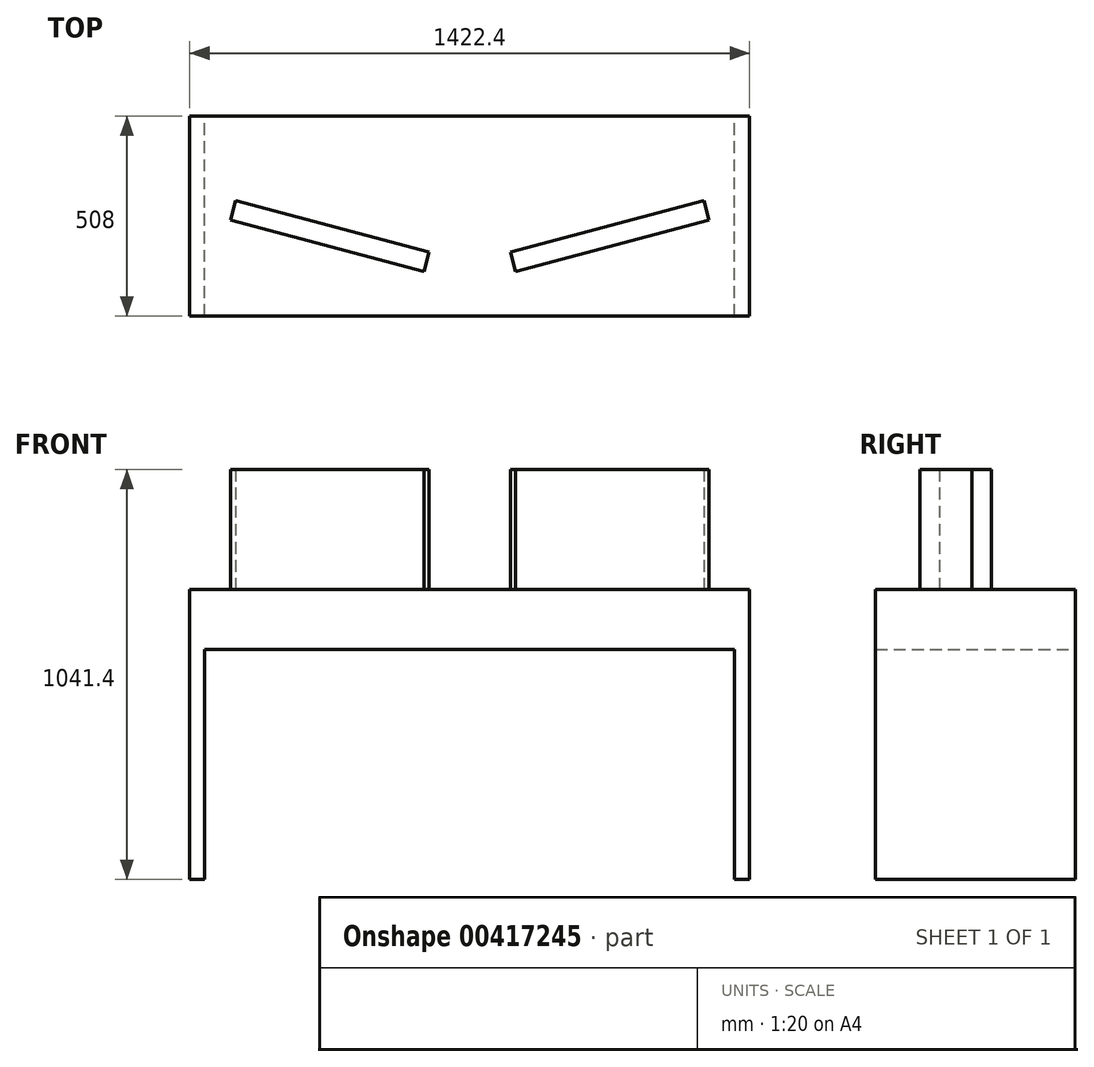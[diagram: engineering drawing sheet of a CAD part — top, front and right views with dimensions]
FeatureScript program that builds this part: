
annotation { "Feature Type Name" : "Feature", "Feature Type Description" : "" }
export const myFeature = defineFeature(function(context is Context, id is Id, definition is map)
    precondition{}
    {
        {
            var Q0;
            Q0=qCreatedBy(makeId("Top.planeOp"),FACE);
            var sketch = newSketch(context, id + "F0", { "sketchPlane" : qUnion([Q0])});
            skLineSegment(sketch, "E0.bottom", {"start": v(0, 0) * mm, "end": v(38.1, 0) * mm});
            skLineSegment(sketch, "E0.top", {"start": v(0, 508) * mm, "end": v(38.1, 508) * mm});
            skLineSegment(sketch, "E0.left", {"start": v(0, 0) * mm, "end": v(0, 508) * mm});
            skLineSegment(sketch, "E0.right", {"start": v(38.1, 0) * mm, "end": v(38.1, 508) * mm});
            skLineSegment(sketch, "E1.bottom", {"start": v(1384.3, 0) * mm, "end": v(1422.4, 0) * mm});
            skLineSegment(sketch, "E1.top", {"start": v(1384.3, 508) * mm, "end": v(1422.4, 508) * mm});
            skLineSegment(sketch, "E1.left", {"start": v(1384.3, 0) * mm, "end": v(1384.3, 508) * mm});
            skLineSegment(sketch, "E1.right", {"start": v(1422.4, 0) * mm, "end": v(1422.4, 508) * mm});
            skLineSegment(sketch, "E2.bottom", {"start": v(0, 0) * mm, "end": v(1422.4, 0) * mm, "construction": true});
            skLineSegment(sketch, "E2.top", {"start": v(0, 508) * mm, "end": v(1422.4, 508) * mm, "construction": true});
            skLineSegment(sketch, "E2.left", {"start": v(0, 0) * mm, "end": v(0, 508) * mm, "construction": true});
            skLineSegment(sketch, "E2.right", {"start": v(1422.4, 0) * mm, "end": v(1422.4, 508) * mm, "construction": true});
            skSolve(sketch);
        }
        {
            var Q0;
            Q0=makeQuery(id+"F0.imprint","IMPRINT",FACE,{"disambiguationData":[TD([[makeQuery(id+"F0.imprint","IMPRINT",EDGE,{"derivedFrom":sQuery(id+"F0.wireOp",EDGE,"E0.bottom")}),1.0]])]});
            var Q1;
            Q1=makeQuery(id+"F0.imprint","IMPRINT",FACE,{"disambiguationData":[TD([[makeQuery(id+"F0.imprint","IMPRINT",EDGE,{"derivedFrom":sQuery(id+"F0.wireOp",EDGE,"E1.bottom")}),1.0]])]});
            extrude(context, id + "F1", {"entities" : qUnion([Q0, Q1]), "depth" : 584.2 * mm});
        }
        {
            var Q0;
            Q0=makeQuery(id+"F1.opExtrude","CAP_FACE",FACE,{"disambiguationData":[OSD([sQuery(id+"F0.wireOp",EDGE,"E0.bottom"),sQuery(id+"F0.wireOp",EDGE,"E0.top"),sQuery(id+"F0.wireOp",EDGE,"E0.left"),sQuery(id+"F0.wireOp",EDGE,"E0.right")])],"isStart":false});
            var sketch = newSketch(context, id + "F2", { "sketchPlane" : qUnion([Q0])});
            skLineSegment(sketch, "E3.bottom", {"start": v(0, 0) * mm, "end": v(1422.4, 0) * mm});
            skLineSegment(sketch, "E3.top", {"start": v(0, 508) * mm, "end": v(1422.4, 508) * mm});
            skLineSegment(sketch, "E3.left", {"start": v(0, 0) * mm, "end": v(0, 508) * mm});
            skLineSegment(sketch, "E3.right", {"start": v(1422.4, 0) * mm, "end": v(1422.4, 508) * mm});
            skPoint(sketch, "E4.0", {"position": v(1422.4, 508) * mm});
            skSolve(sketch);
        }
        {
            var Q0;
            {var subQ2=sQuery(id+"F2.wireOp",EDGE,"E3.right");Q0=makeQuery(id+"F2.imprint","IMPRINT",FACE,{"disambiguationData":[TD([[makeQuery(id+"F2.imprint","IMPRINT",EDGE,{"derivedFrom":subQ2}),1.0]])]});}
            var Q1;
            {var subQ0=sQuery(id+"F2.wireOp",EDGE,"E3.left");Q1=makeQuery(id+"F2.imprint","IMPRINT",FACE,{"disambiguationData":[TD([[makeQuery(id+"F2.imprint","IMPRINT",EDGE,{"derivedFrom":subQ0}),-1.0]])]});}
            extrude(context, id + "F3", {"entities" : qUnion([Q0, Q1]), "operationType" : NewBodyOperationType.ADD, "depth" : 152.4 * mm});
        }
        {
            var Q0;
            Q0=makeQuery(id+"F3.opExtrude","CAP_FACE",FACE,{"disambiguationData":[OSD([sQuery(id+"F2.wireOp",EDGE,"E3.bottom"),sQuery(id+"F2.wireOp",EDGE,"E3.top"),sQuery(id+"F2.wireOp",EDGE,"E3.left"),sQuery(id+"F2.wireOp",EDGE,"E3.right")])],"isStart":false});
            var sketch = newSketch(context, id + "F4", { "sketchPlane" : qUnion([Q0])});
            skLineSegment(sketch, "E5.bottom", {"start": v(607.52, 162) * mm, "end": v(116.83, 293.47) * mm});
            skLineSegment(sketch, "E5.top", {"start": v(594.37, 112.93) * mm, "end": v(103.68, 244.4) * mm});
            skLineSegment(sketch, "E5.left", {"start": v(607.52, 162) * mm, "end": v(594.37, 112.93) * mm});
            skLineSegment(sketch, "E5.right", {"start": v(116.83, 293.47) * mm, "end": v(103.68, 244.4) * mm});
            skPoint(sketch, "E5.middle", {"position": v(355.6, 203.2) * mm});
            skLineSegment(sketch, "E6.bottom", {"start": v(1305.57, 293.47) * mm, "end": v(814.88, 162) * mm});
            skLineSegment(sketch, "E6.top", {"start": v(1318.72, 244.4) * mm, "end": v(828.03, 112.93) * mm});
            skLineSegment(sketch, "E6.left", {"start": v(1305.57, 293.47) * mm, "end": v(1318.72, 244.4) * mm});
            skLineSegment(sketch, "E6.right", {"start": v(814.88, 162) * mm, "end": v(828.03, 112.93) * mm});
            skPoint(sketch, "E6.middle", {"position": v(1066.8, 203.2) * mm});
            skLineSegment(sketch, "E7", {"start": v(355.6, 0) * mm, "end": v(355.6, 203.2) * mm, "construction": true});
            skLineSegment(sketch, "E8", {"start": v(1066.8, 0) * mm, "end": v(1066.8, 203.2) * mm, "construction": true});
            skSolve(sketch);
        }
        {
            var Q0;
            Q0=makeQuery(id+"F4.imprint","IMPRINT",FACE,{"disambiguationData":[TD([[makeQuery(id+"F4.imprint","IMPRINT",EDGE,{"derivedFrom":sQuery(id+"F4.wireOp",EDGE,"E5.bottom")}),1.0]])]});
            var Q1;
            Q1=makeQuery(id+"F4.imprint","IMPRINT",FACE,{"disambiguationData":[TD([[makeQuery(id+"F4.imprint","IMPRINT",EDGE,{"derivedFrom":sQuery(id+"F4.wireOp",EDGE,"E6.bottom")}),1.0]])]});
            extrude(context, id + "F5", {"entities" : qUnion([Q0, Q1]), "operationType" : NewBodyOperationType.ADD, "depth" : 304.8 * mm});
        }
    });
